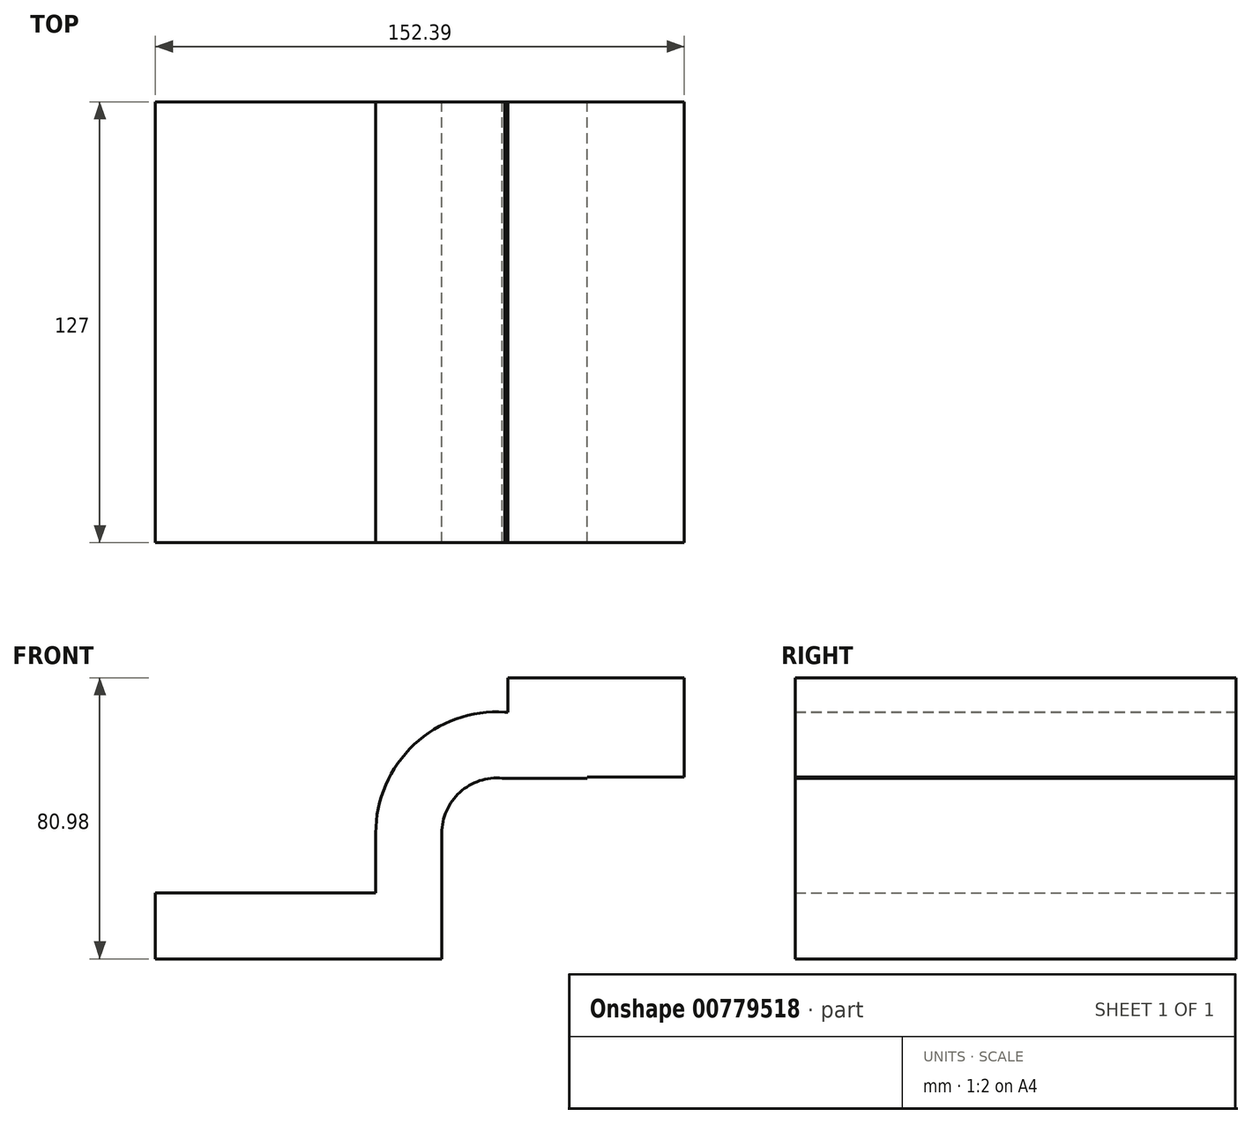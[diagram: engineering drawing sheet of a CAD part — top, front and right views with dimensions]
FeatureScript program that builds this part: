
annotation { "Feature Type Name" : "Feature", "Feature Type Description" : "" }
export const myFeature = defineFeature(function(context is Context, id is Id, definition is map)
    precondition{}
    {
        {
            var Q0;
            Q0=qCreatedBy(makeId("Front.planeOp"),FACE);
            var sketch = newSketch(context, id + "F0", { "sketchPlane" : qUnion([Q0])});
            skLineSegment(sketch, "E0.bottom", {"start": v(-41.28, 9.52) * mm, "end": v(41.28, 9.53) * mm});
            skLineSegment(sketch, "E0.top", {"start": v(-41.28, -9.53) * mm, "end": v(41.28, -9.53) * mm});
            skLineSegment(sketch, "E0.left", {"start": v(-41.28, 9.52) * mm, "end": v(-41.28, -9.53) * mm});
            skLineSegment(sketch, "E0.right", {"start": v(41.28, 9.53) * mm, "end": v(41.28, -9.52) * mm});
            skPoint(sketch, "E0.middle", {"position": v(0, 0) * mm});
            skLineSegment(sketch, "E1.bottom", {"start": v(111.12, 42.88) * mm, "end": v(60.32, 42.88) * mm});
            skLineSegment(sketch, "E1.top", {"start": v(111.12, 71.45) * mm, "end": v(60.32, 71.45) * mm});
            skLineSegment(sketch, "E1.left", {"start": v(111.12, 42.88) * mm, "end": v(111.12, 71.45) * mm});
            skLineSegment(sketch, "E1.right", {"start": v(60.32, 42.88) * mm, "end": v(60.32, 71.45) * mm});
            skPoint(sketch, "E1.middle", {"position": v(85.72, 57.16) * mm});
            skLineSegment(sketch, "E2", {"start": v(41.27, 9.53) * mm, "end": v(41.27, 26.72) * mm});
            skArc(sketch, "E3", {"start": v(41.27, 26.72) * mm, "mid": v(46.48, 38.48) * mm, "end": v(58.69, 42.52) * mm});
            skLineSegment(sketch, "E4", {"start": v(58.69, 42.52) * mm, "end": v(83.18, 42.52) * mm});
            skLineSegment(sketch, "E5.0", {"start": v(59.43, 61.57) * mm, "end": v(83.18, 61.57) * mm});
            skArc(sketch, "E5.1", {"start": v(22.22, 26.72) * mm, "mid": v(33.27, 52.21) * mm, "end": v(59.43, 61.57) * mm});
            skLineSegment(sketch, "E5.2", {"start": v(22.22, 9.53) * mm, "end": v(22.22, 26.72) * mm});
            skLineSegment(sketch, "E6", {"start": v(83.18, 42.52) * mm, "end": v(83.18, 61.57) * mm});
            skFitSpline(sketch, "E7", {"points": [v(-41.28, 9.52) * mm, v(59.43, 61.57) * mm, v(83.18, 42.52) * mm], "startDerivative": vector(180.33, 123.43) * mm, "endDerivative": vector(55.35, -78.82) * mm});
            skSolve(sketch);
        }
        {
            var Q0;
            {var subQ1=sQuery(id+"F0.wireOp",EDGE,"E1.top");Q0=makeQuery(id+"F0.imprint","IMPRINT",FACE,{"disambiguationData":[TD([[makeQuery(id+"F0.imprint","IMPRINT",EDGE,{"derivedFrom":subQ1}),1.0]])]});}
            var Q1;
            Q1=makeQuery(id+"F0.imprint","IMPRINT",FACE,{"disambiguationData":[TD([[makeQuery(id+"F0.imprint","IMPRINT",EDGE,{"derivedFrom":sQuery(id+"F0.wireOp",EDGE,"E0.top")}),1.0]])]});
            var Q2;
            {var subQ4=sQuery(id+"F0.wireOp",EDGE,"E5.1");Q2=makeQuery(id+"F0.imprint","IMPRINT",FACE,{"disambiguationData":[TD([[makeQuery(id+"F0.imprint","IMPRINT",EDGE,{"derivedFrom":subQ4}),1.0]])]});}
            var Q3;
            {var subQ0=sQuery(id+"F0.wireOp",EDGE,"E6");var subQ1=sQuery(id+"F0.wireOp",EDGE,"E1.bottom");var subQ2=makeQuery(id+"F0.imprint","INTERSECT",VERTEX,{"derivedFrom":[subQ1,subQ0]});Q3=makeQuery(id+"F0.imprint","IMPRINT",FACE,{"disambiguationData":[TD([[makeQuery(id+"F0.imprint","IMPRINT",EDGE,{"disambiguationData":[TD([[subQ2,-1.0]])],"derivedFrom":subQ1}),1.0]])]});}
            var Q4;
            {var subQ0=sQuery(id+"F0.wireOp",EDGE,"E5.0");var subQ1=sQuery(id+"F0.wireOp",EDGE,"E1.right");var subQ2=makeQuery(id+"F0.imprint","INTERSECT",VERTEX,{"derivedFrom":[subQ1,subQ0]});Q4=makeQuery(id+"F0.imprint","IMPRINT",FACE,{"disambiguationData":[TD([[makeQuery(id+"F0.imprint","IMPRINT",EDGE,{"disambiguationData":[TD([[subQ2,1.0]])],"derivedFrom":subQ1}),1.0]])]});}
            var Q5;
            {var subQ0=sQuery(id+"F0.wireOp",EDGE,"E6");var subQ5=sQuery(id+"F0.wireOp",EDGE,"E1.bottom");var subQ6=makeQuery(id+"F0.imprint","INTERSECT",VERTEX,{"derivedFrom":[subQ5,subQ0]});Q5=makeQuery(id+"F0.imprint","IMPRINT",FACE,{"disambiguationData":[TD([[makeQuery(id+"F0.imprint","IMPRINT",EDGE,{"disambiguationData":[TD([[subQ6,-1.0]])],"derivedFrom":subQ5}),-1.0]])]});}
            var Q6;
            {var subQ0=sQuery(id+"F0.wireOp",EDGE,"E2");Q6=makeQuery(id+"F0.imprint","IMPRINT",FACE,{"disambiguationData":[TD([[makeQuery(id+"F0.imprint","IMPRINT",EDGE,{"derivedFrom":subQ0}),1.0]])]});}
            var Q7;
            {var subQ0=sQuery(id+"F0.wireOp",EDGE,"E1.right");var subQ1=sQuery(id+"F0.wireOp",EDGE,"E1.bottom");var subQ2=makeQuery(id+"F0.imprint","INTERSECT",VERTEX,{"derivedFrom":[subQ1,subQ0]});Q7=makeQuery(id+"F0.imprint","IMPRINT",FACE,{"disambiguationData":[TD([[makeQuery(id+"F0.imprint","IMPRINT",EDGE,{"disambiguationData":[TD([[subQ2,1.0]])],"derivedFrom":subQ1}),-1.0]])]});}
            extrude(context, id + "F1", {"entities" : qUnion([Q0, Q1, Q2, Q3, Q4, Q5, Q6, Q7]), "endBound" : BoundingType.SYMMETRIC, "depth" : 127 * mm, "offsetDistance" : 25.4 * mm});
        }
    });
